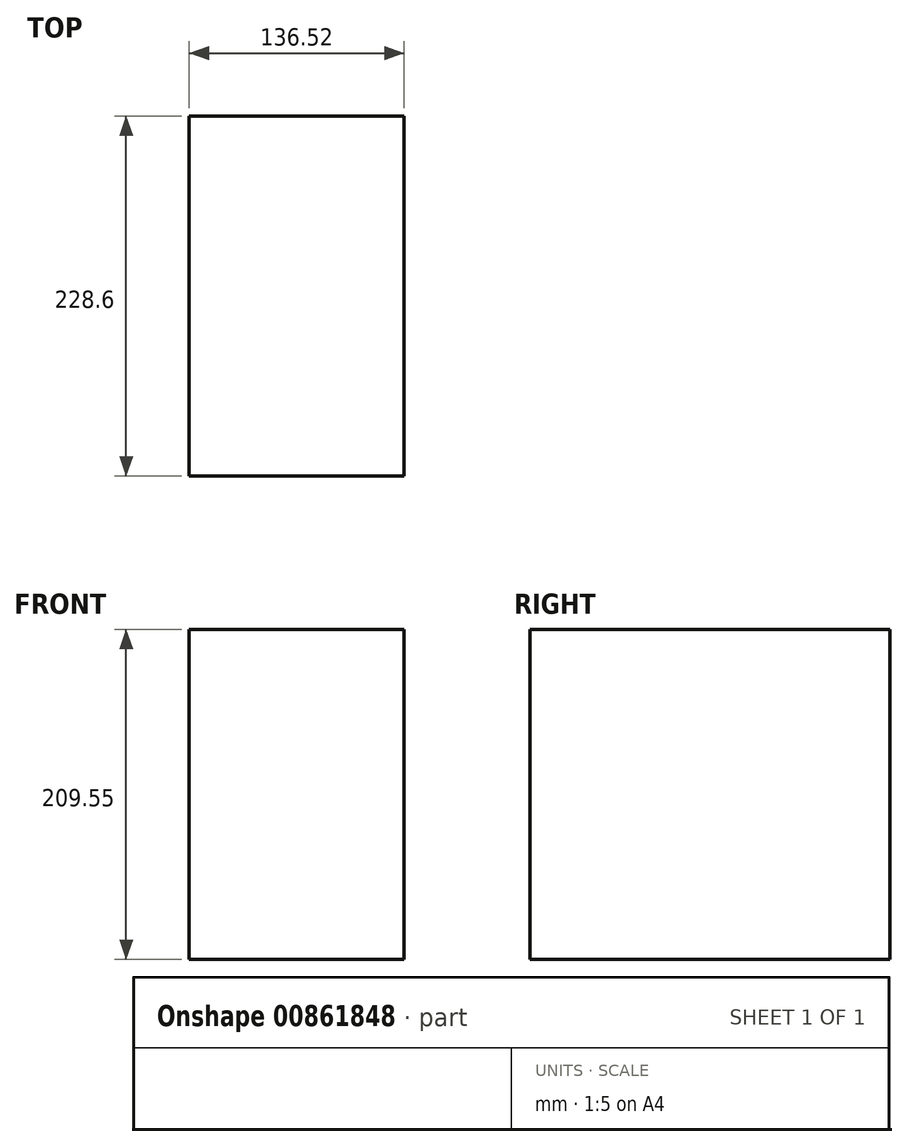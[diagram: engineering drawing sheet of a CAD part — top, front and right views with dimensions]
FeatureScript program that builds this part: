
annotation { "Feature Type Name" : "Feature", "Feature Type Description" : "" }
export const myFeature = defineFeature(function(context is Context, id is Id, definition is map)
    precondition{}
    {
        {
            var Q0;
            Q0=qCreatedBy(makeId("Top.planeOp"),FACE);
            var sketch = newSketch(context, id + "F0", { "sketchPlane" : qUnion([Q0])});
            skLineSegment(sketch, "E0.bottom", {"start": v(68.26, 114.3) * mm, "end": v(-68.26, 114.3) * mm});
            skLineSegment(sketch, "E0.top", {"start": v(68.26, -114.3) * mm, "end": v(-68.26, -114.3) * mm});
            skLineSegment(sketch, "E0.left", {"start": v(68.26, 114.3) * mm, "end": v(68.26, -114.3) * mm});
            skLineSegment(sketch, "E0.right", {"start": v(-68.26, 114.3) * mm, "end": v(-68.26, -114.3) * mm});
            skPoint(sketch, "E0.middle", {"position": v(0, 0) * mm});
            skSolve(sketch);
        }
        {
            var Q0;
            Q0=makeQuery(id+"F0.imprint","IMPRINT",FACE,{"disambiguationData":[TD([[makeQuery(id+"F0.imprint","IMPRINT",EDGE,{"derivedFrom":sQuery(id+"F0.wireOp",EDGE,"E0.bottom")}),1.0]])]});
            extrude(context, id + "F1", {"entities" : qUnion([Q0]), "depth" : 209.55 * mm, "offsetDistance" : 25.4 * mm});
        }
    });
